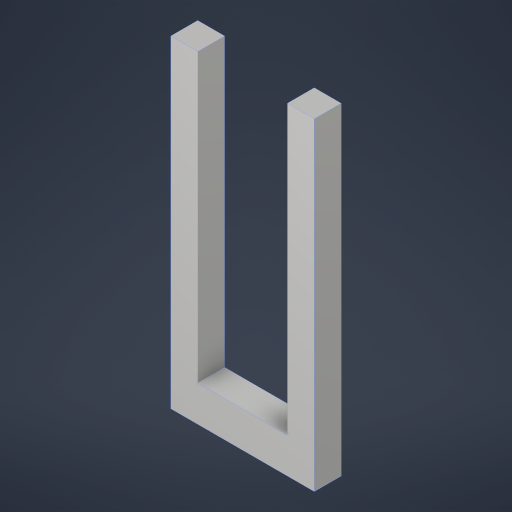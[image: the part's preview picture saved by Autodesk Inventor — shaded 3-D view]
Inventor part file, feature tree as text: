
AUTODESK INVENTOR PART (.ipt)
format: ipt  version: 2024.2 (Build 282272000, 272)  size: 178,688 bytes
history: native  units: in
note: dims shown in document units (in); Inventor stores cm internally (conversion verified against a paired STEP export)
features: extrude x2, sketch x2, projected_geometry x1
ambient origin geometry x8: Origin, YZ Plane, XZ Plane, XY Plane, X Axis, Y Axis, Z Axis, Center Point
bodies: Solid1 (feature_tree)
feature tree (5):
  extrude  "Extrusion1"  Depth=36.0in
  extrude  "Extrusion2"  Depth=4.0in
  sketch  "Sketch1"  dims[d0=16.0in d1=36.0in]
  sketch  "Sketch2"  dims[d2=3.0in d3=0.0in d4=4.0in d5=3.0in d6=3.0in d7=1.0in d8=0.0in]
  projected_geometry  "Project Cut Edges1"
